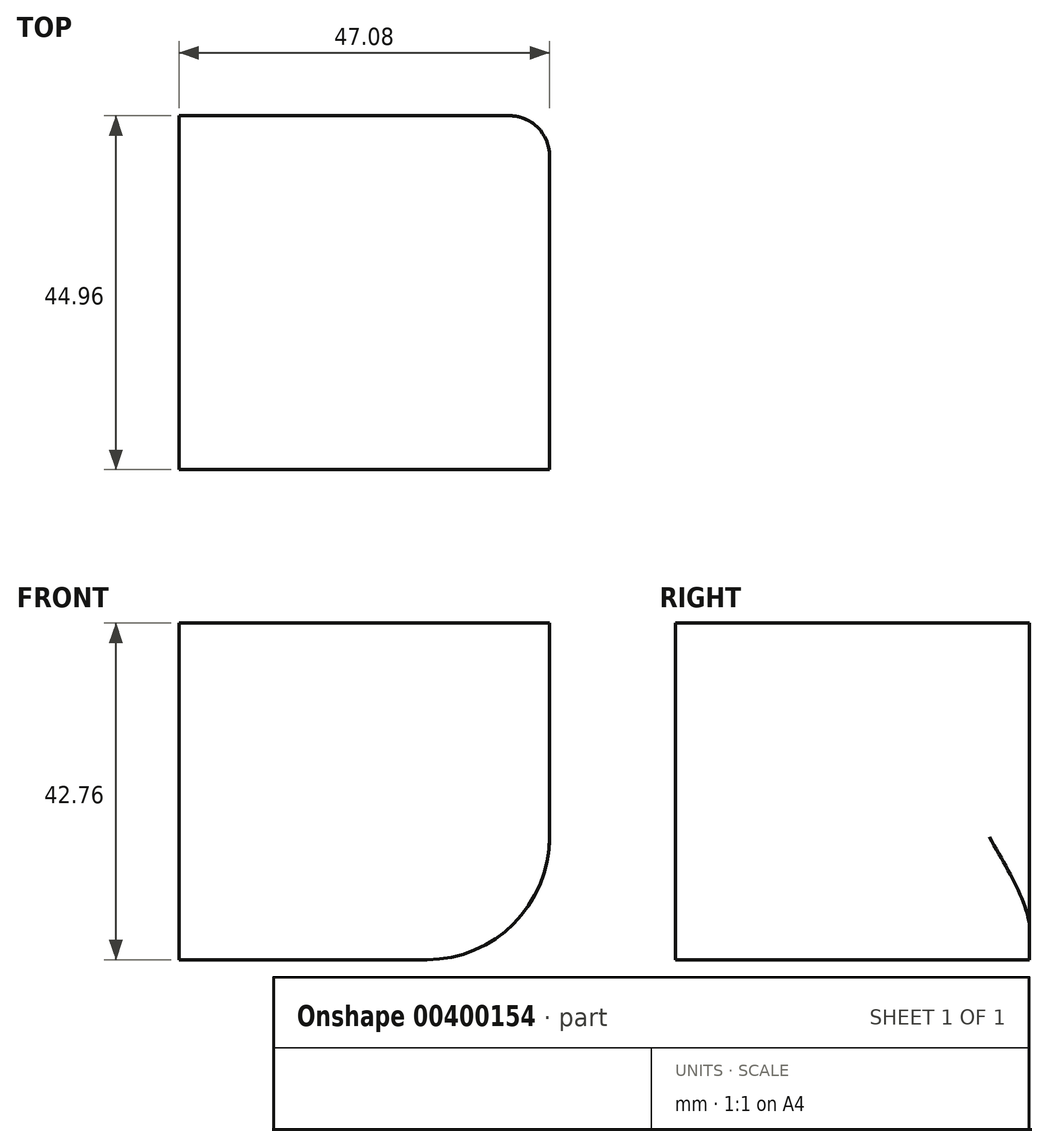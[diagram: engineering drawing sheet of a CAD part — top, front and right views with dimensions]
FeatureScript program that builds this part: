
annotation { "Feature Type Name" : "Feature", "Feature Type Description" : "" }
export const myFeature = defineFeature(function(context is Context, id is Id, definition is map)
    precondition{}
    {
        {
            var Q0;
            Q0=qCreatedBy(makeId("Front.planeOp"),FACE);
            var sketch = newSketch(context, id + "F0", { "sketchPlane" : qUnion([Q0])});
            skLineSegment(sketch, "E0.bottom", {"start": v(-11.29, 14.25) * mm, "end": v(35.8, 14.25) * mm});
            skLineSegment(sketch, "E0.top", {"start": v(-11.29, -28.5) * mm, "end": v(20.21, -28.5) * mm});
            skLineSegment(sketch, "E0.left", {"start": v(-11.29, 14.25) * mm, "end": v(-11.29, -28.5) * mm});
            skLineSegment(sketch, "E0.right", {"start": v(35.8, 14.25) * mm, "end": v(35.8, -12.92) * mm});
            skArc(sketch, "E1", {"start": v(20.21, -28.5) * mm, "mid": v(31.23, -23.94) * mm, "end": v(35.8, -12.92) * mm});
            skSolve(sketch);
        }
        {
            var Q0;
            Q0=makeQuery(id+"F0.imprint","IMPRINT",FACE,{"disambiguationData":[TD([[makeQuery(id+"F0.imprint","IMPRINT",EDGE,{"derivedFrom":sQuery(id+"F0.wireOp",EDGE,"E0.bottom")}),-1.0]])]});
            extrude(context, id + "F1", {"entities" : qUnion([Q0]), "depth" : 44.96 * mm});
        }
        {
            var Q0;
            Q0=makeQuery(id+"F1.opExtrude","CAP_EDGE",EDGE,{"disambiguationData":[OSD([sQuery(id+"F0.wireOp",EDGE,"E0.right")])],"isStart":true});
            fillet(context, id + "F2", {"entities" : qUnion([Q0]), "radius" : 5.08 * mm, "allowEdgeOverflow" : false});
        }
    });
